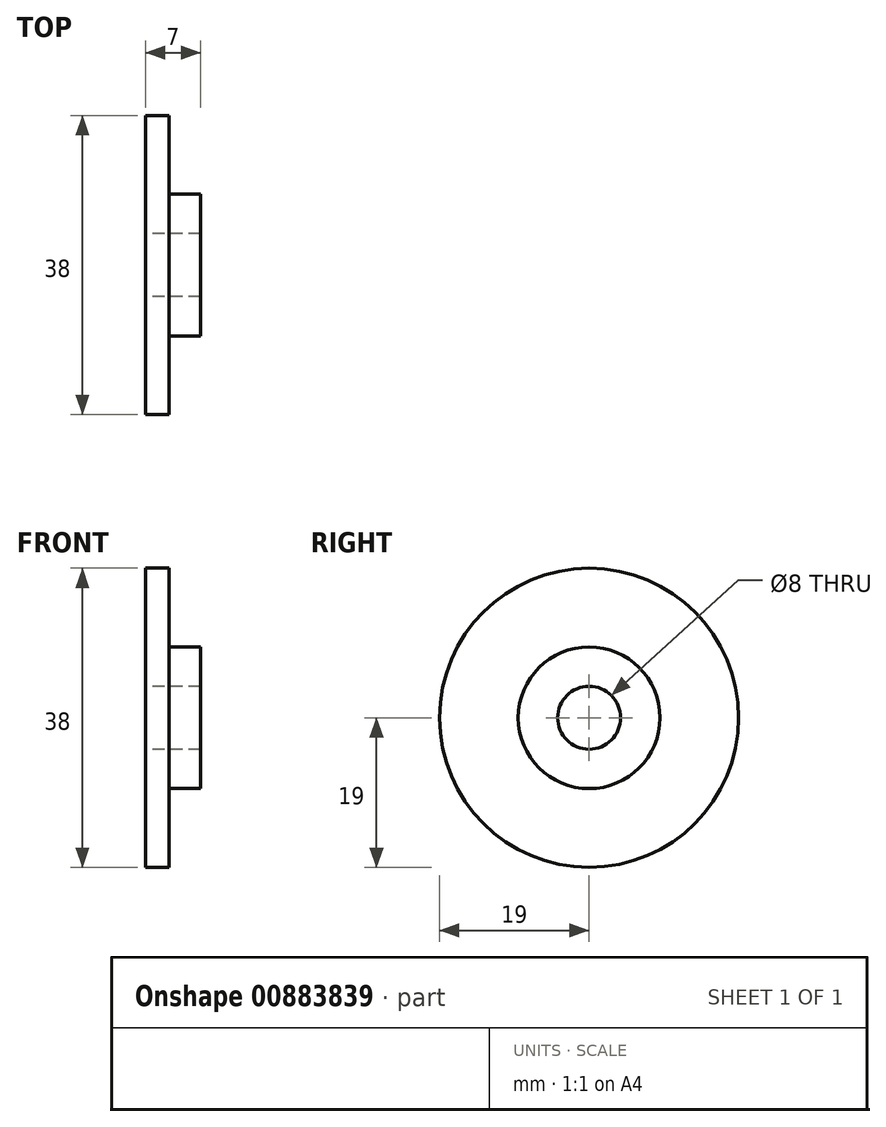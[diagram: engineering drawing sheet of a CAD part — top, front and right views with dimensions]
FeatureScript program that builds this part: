
annotation { "Feature Type Name" : "Feature", "Feature Type Description" : "" }
export const myFeature = defineFeature(function(context is Context, id is Id, definition is map)
    precondition{}
    {
        {
            var Q0;
            Q0=qCreatedBy(makeId("Top.planeOp"),FACE);
            var sketch = newSketch(context, id + "F0", { "sketchPlane" : qUnion([Q0])});
            skLineSegment(sketch, "E0.bottom", {"start": v(0, 19) * mm, "end": v(3, 19) * mm});
            skLineSegment(sketch, "E0.top", {"start": v(0, 4) * mm, "end": v(3, 4) * mm});
            skLineSegment(sketch, "E0.left", {"start": v(0, 19) * mm, "end": v(0, 4) * mm});
            skLineSegment(sketch, "E0.right", {"start": v(3, 19) * mm, "end": v(3, 4) * mm});
            skLineSegment(sketch, "E1.bottom", {"start": v(3, 4) * mm, "end": v(7, 4) * mm});
            skLineSegment(sketch, "E1.top", {"start": v(3, 9) * mm, "end": v(7, 9) * mm});
            skLineSegment(sketch, "E1.left", {"start": v(3, 4) * mm, "end": v(3, 9) * mm});
            skLineSegment(sketch, "E1.right", {"start": v(7, 4) * mm, "end": v(7, 9) * mm});
            skLineSegment(sketch, "E2", {"start": v(0, 0) * mm, "end": v(18.78, 0) * mm});
            skSolve(sketch);
        }
        {
            var Q0;
            Q0=makeQuery(id+"F0.imprint","IMPRINT",FACE,{"disambiguationData":[TD([[makeQuery(id+"F0.imprint","IMPRINT",EDGE,{"derivedFrom":sQuery(id+"F0.wireOp",EDGE,"E0.bottom")}),-1.0]])]});
            var Q1;
            Q1=makeQuery(id+"F0.imprint","IMPRINT",FACE,{"disambiguationData":[TD([[makeQuery(id+"F0.imprint","IMPRINT",EDGE,{"derivedFrom":sQuery(id+"F0.wireOp",EDGE,"E1.bottom")}),1.0]])]});
            var Q2;
            Q2=sQuery(id+"F0.wireOp",EDGE,"E2");
            revolve(context, id + "F1", {"surfaceOperationType" : NewSurfaceOperationType.NEW, "entities" : qUnion([Q0, Q1]), "axis" : qUnion([Q2]), "revolveType" : RevolveType.FULL});
        }
    });
